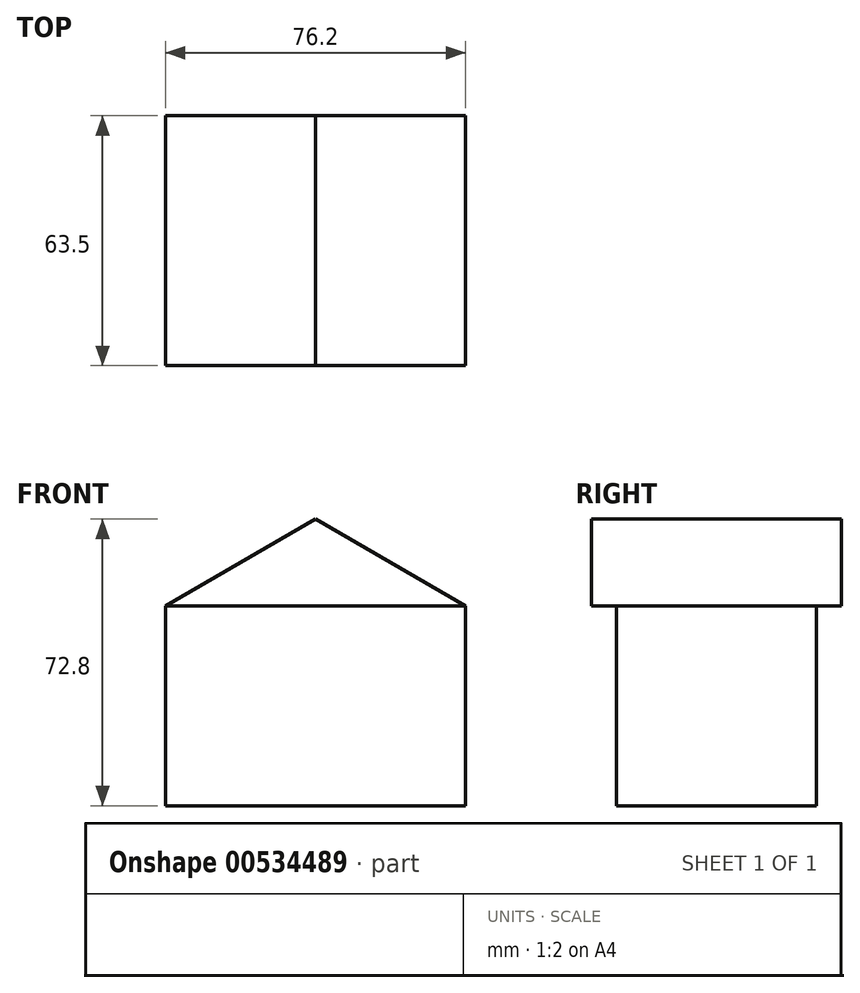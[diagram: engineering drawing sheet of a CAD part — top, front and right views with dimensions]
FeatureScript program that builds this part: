
annotation { "Feature Type Name" : "Feature", "Feature Type Description" : "" }
export const myFeature = defineFeature(function(context is Context, id is Id, definition is map)
    precondition{}
    {
        {
            var Q0;
            Q0=qCreatedBy(makeId("Front.planeOp"),FACE);
            var sketch = newSketch(context, id + "F0", { "sketchPlane" : qUnion([Q0])});
            skLineSegment(sketch, "E0.bottom", {"start": v(-38.1, 25.4) * mm, "end": v(38.1, 25.4) * mm});
            skLineSegment(sketch, "E0.top", {"start": v(-38.1, -25.4) * mm, "end": v(38.1, -25.4) * mm});
            skLineSegment(sketch, "E0.left", {"start": v(-38.1, 25.4) * mm, "end": v(-38.1, -25.4) * mm});
            skLineSegment(sketch, "E0.right", {"start": v(38.1, 25.4) * mm, "end": v(38.1, -25.4) * mm});
            skPoint(sketch, "E0.middle", {"position": v(0, 0) * mm});
            skLineSegment(sketch, "E1", {"start": v(-38.1, 25.4) * mm, "end": v(0, 47.4) * mm});
            skLineSegment(sketch, "E2", {"start": v(38.1, 25.4) * mm, "end": v(0, 47.4) * mm});
            skSolve(sketch);
        }
        {
            var Q0;
            Q0=makeQuery(id+"F0.imprint","IMPRINT",FACE,{"disambiguationData":[TD([[makeQuery(id+"F0.imprint","IMPRINT",EDGE,{"derivedFrom":sQuery(id+"F0.wireOp",EDGE,"E0.bottom")}),-1.0]])]});
            extrude(context, id + "F1", {"entities" : qUnion([Q0]), "endBound" : BoundingType.SYMMETRIC, "depth" : 50.8 * mm, "offsetDistance" : 25.4 * mm});
        }
        {
            var Q0;
            Q0=makeQuery(id+"F0.imprint","IMPRINT",FACE,{"disambiguationData":[TD([[makeQuery(id+"F0.imprint","IMPRINT",EDGE,{"derivedFrom":sQuery(id+"F0.wireOp",EDGE,"E0.bottom")}),1.0]])]});
            extrude(context, id + "F2", {"entities" : qUnion([Q0]), "operationType" : NewBodyOperationType.ADD, "endBound" : BoundingType.SYMMETRIC, "depth" : 63.5 * mm, "offsetDistance" : 25.4 * mm});
        }
    });
